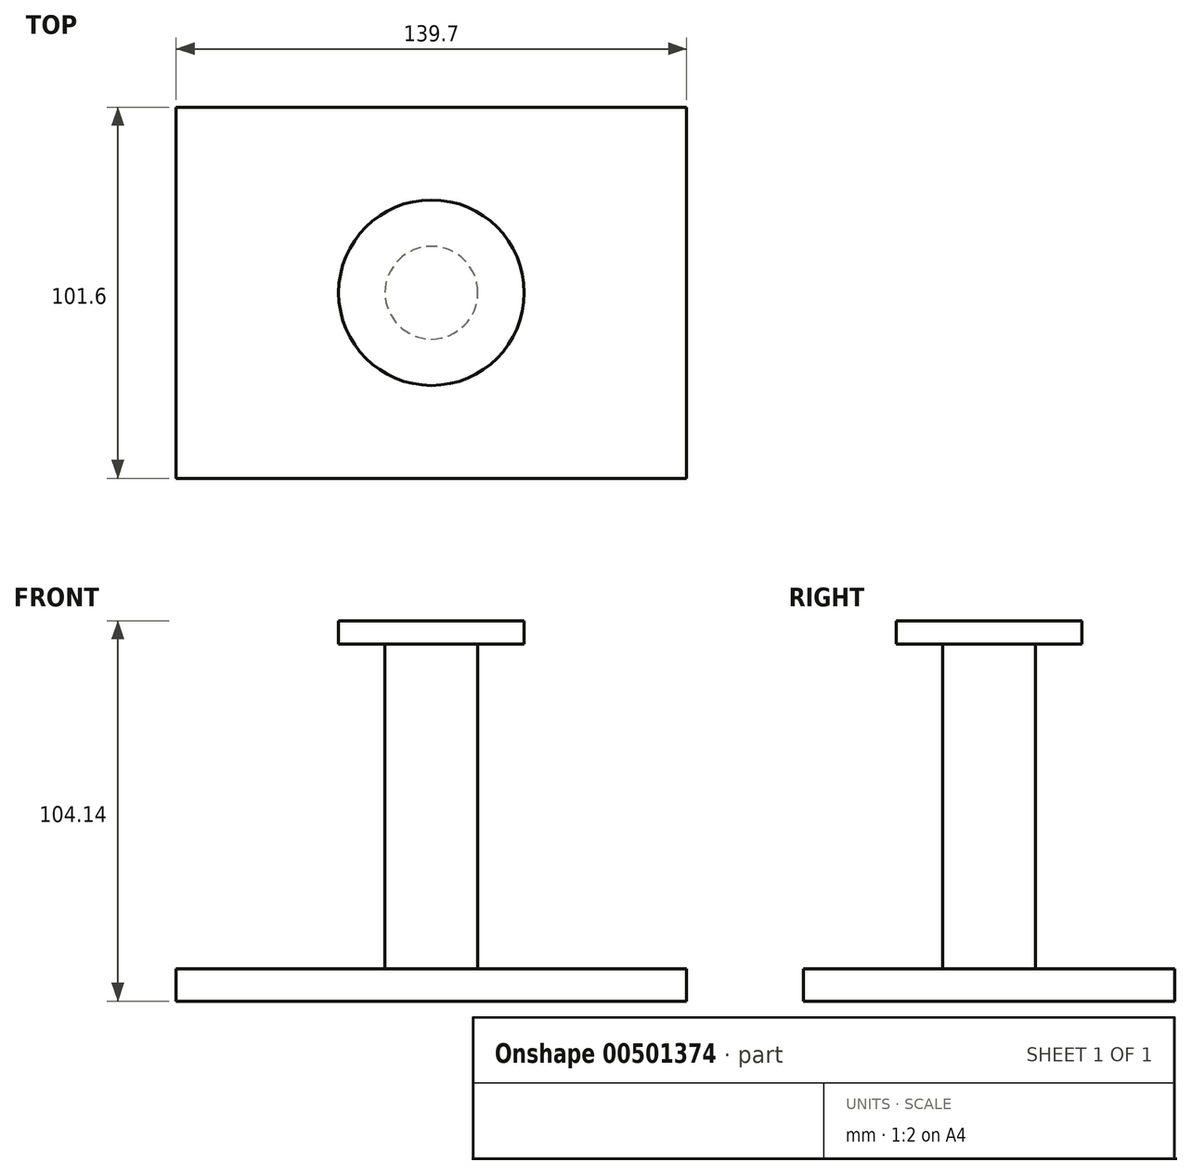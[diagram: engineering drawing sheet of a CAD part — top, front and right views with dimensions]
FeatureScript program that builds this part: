
annotation { "Feature Type Name" : "Feature", "Feature Type Description" : "" }
export const myFeature = defineFeature(function(context is Context, id is Id, definition is map)
    precondition{}
    {
        {
            var Q0;
            Q0=qCreatedBy(makeId("Top.planeOp"),FACE);
            var sketch = newSketch(context, id + "F0", { "sketchPlane" : qUnion([Q0])});
            skCircle(sketch, "E0", {"center": v(0, 0) * mm, "radius": 25.4 * mm});
            skSolve(sketch);
        }
        {
            var Q0;
            Q0=qSketchRegion(id+"F0",true);
            extrude(context, id + "F1", {"entities" : qUnion([Q0]), "oppositeDirection" : true, "depth" : 6.35 * mm});
        }
        {
            var Q0;
            Q0=makeQuery(id+"F1.opExtrude","CAP_FACE",FACE,{"disambiguationData":[OSD([sQuery(id+"F0.wireOp",EDGE,"E0")])],"isStart":false});
            var sketch = newSketch(context, id + "F2", { "sketchPlane" : qUnion([Q0])});
            skCircle(sketch, "E1", {"center": v(0, 0) * mm, "radius": 12.7 * mm});
            skSolve(sketch);
        }
        {
            var Q0;
            Q0=qSketchRegion(id+"F2",true);
            extrude(context, id + "F3", {"entities" : qUnion([Q0]), "operationType" : NewBodyOperationType.ADD, "depth" : 88.9 * mm});
        }
        {
            var Q0;
            Q0=makeQuery(id+"F3.opExtrude","CAP_FACE",FACE,{"disambiguationData":[OSD([sQuery(id+"F2.wireOp",EDGE,"E1")])],"isStart":false});
            var sketch = newSketch(context, id + "F4", { "sketchPlane" : qUnion([Q0])});
            skLineSegment(sketch, "E2.bottom", {"start": v(69.85, -50.8) * mm, "end": v(-69.85, -50.8) * mm});
            skLineSegment(sketch, "E2.top", {"start": v(69.85, 50.8) * mm, "end": v(-69.85, 50.8) * mm});
            skLineSegment(sketch, "E2.left", {"start": v(69.85, -50.8) * mm, "end": v(69.85, 50.8) * mm});
            skLineSegment(sketch, "E2.right", {"start": v(-69.85, -50.8) * mm, "end": v(-69.85, 50.8) * mm});
            skPoint(sketch, "E2.middle", {"position": v(0, 0) * mm});
            skSolve(sketch);
        }
        {
            var Q0;
            Q0=qSketchRegion(id+"F4",true);
            extrude(context, id + "F5", {"entities" : qUnion([Q0]), "operationType" : NewBodyOperationType.ADD, "depth" : 8.9 * mm});
        }
    });
